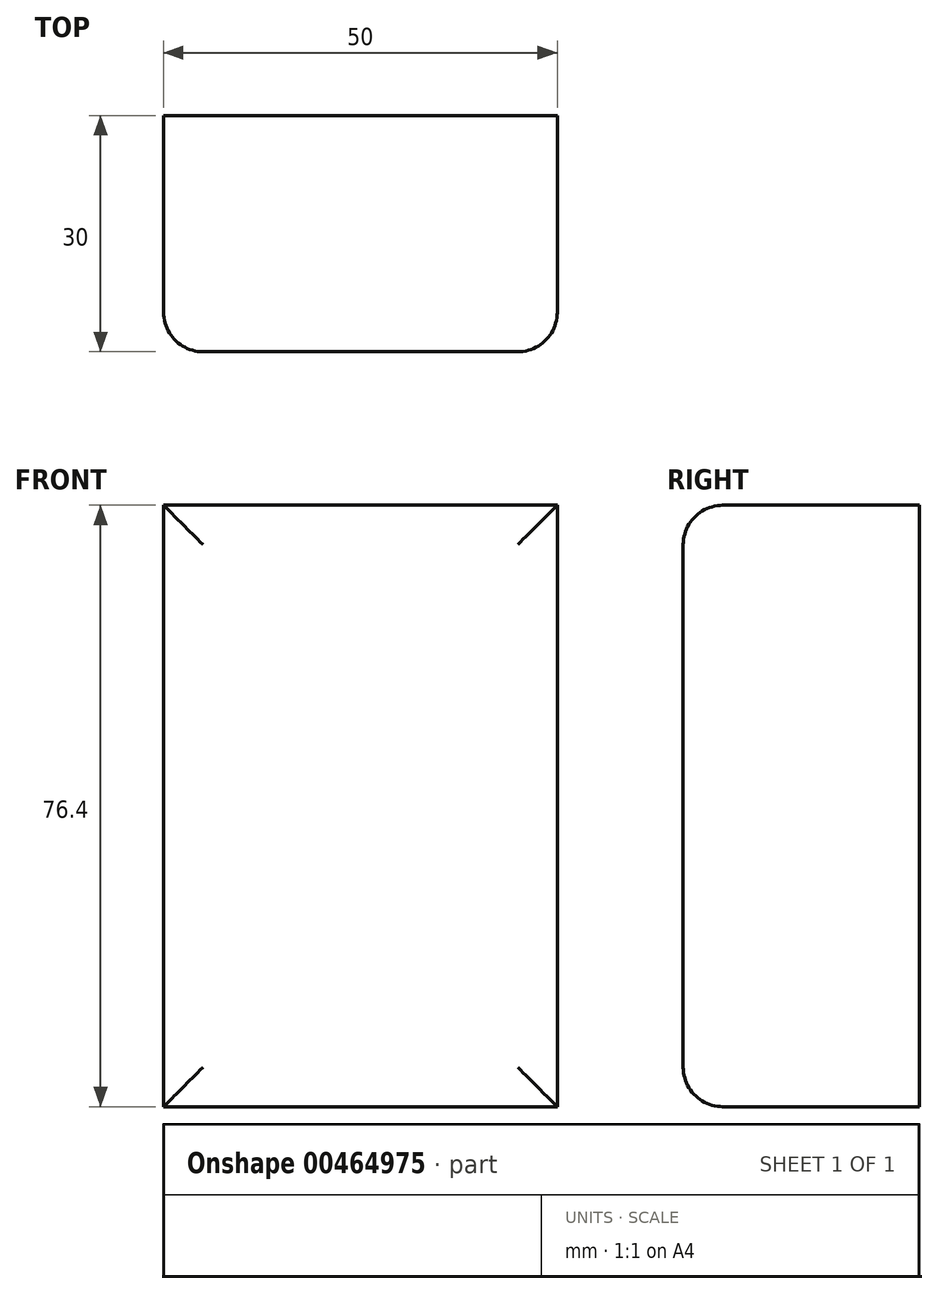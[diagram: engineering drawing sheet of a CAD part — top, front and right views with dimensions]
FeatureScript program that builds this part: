
annotation { "Feature Type Name" : "Feature", "Feature Type Description" : "" }
export const myFeature = defineFeature(function(context is Context, id is Id, definition is map)
    precondition{}
    {
        {
            var Q0;
            Q0=qCreatedBy(makeId("Top.planeOp"),FACE);
            var sketch = newSketch(context, id + "F0", { "sketchPlane" : qUnion([Q0])});
            skLineSegment(sketch, "E0.bottom", {"start": v(25, 15) * mm, "end": v(-25, 15) * mm});
            skLineSegment(sketch, "E0.top", {"start": v(25, -15) * mm, "end": v(-25, -15) * mm});
            skLineSegment(sketch, "E0.left", {"start": v(25, 15) * mm, "end": v(25, -15) * mm});
            skLineSegment(sketch, "E0.right", {"start": v(-25, 15) * mm, "end": v(-25, -15) * mm});
            skPoint(sketch, "E0.middle", {"position": v(0, 0) * mm});
            skSolve(sketch);
        }
        {
            var Q0;
            Q0=makeQuery(id+"F0.imprint","IMPRINT",FACE,{"disambiguationData":[TD([[makeQuery(id+"F0.imprint","IMPRINT",EDGE,{"derivedFrom":sQuery(id+"F0.wireOp",EDGE,"E0.bottom")}),1.0]])]});
            extrude(context, id + "F1", {"entities" : qUnion([Q0]), "depth" : 76.4 * mm});
        }
        {
            var Q0;
            Q0=makeQuery(id+"F1.opExtrude","SWEPT_FACE",FACE,{"disambiguationData":[OSD([sQuery(id+"F0.wireOp",EDGE,"E0.top")])]});
            fillet(context, id + "F2", {"entities" : qUnion([Q0]), "radius" : 5 * mm, "tangentPropagation" : true, "allowEdgeOverflow" : false});
        }
    });
